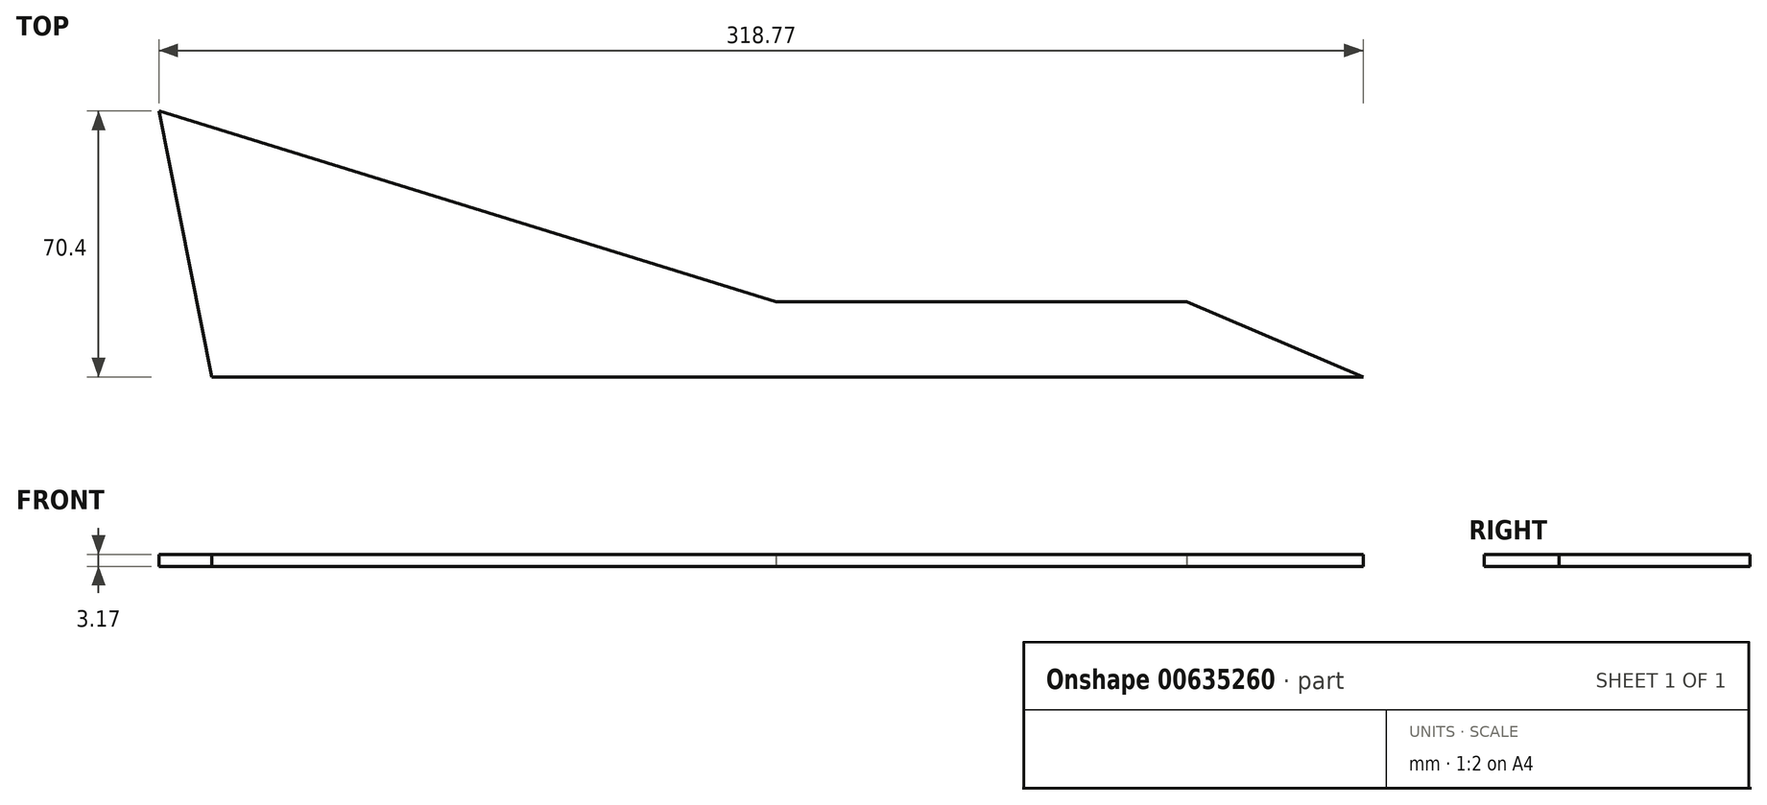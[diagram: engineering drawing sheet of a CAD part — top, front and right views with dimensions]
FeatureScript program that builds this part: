
annotation { "Feature Type Name" : "Feature", "Feature Type Description" : "" }
export const myFeature = defineFeature(function(context is Context, id is Id, definition is map)
    precondition{}
    {
        {
            var Q0;
            Q0=qCreatedBy(makeId("Top.planeOp"),FACE);
            var sketch = newSketch(context, id + "F0", { "sketchPlane" : qUnion([Q0])});
            skLineSegment(sketch, "E0", {"start": v(0, 0) * mm, "end": v(-304.8, 0) * mm});
            skLineSegment(sketch, "E1", {"start": v(-304.8, 0) * mm, "end": v(-318.77, 70.4) * mm});
            skLineSegment(sketch, "E2", {"start": v(-318.77, 70.4) * mm, "end": v(-155.47, 19.85) * mm});
            skLineSegment(sketch, "E3", {"start": v(-155.47, 19.85) * mm, "end": v(-46.76, 19.85) * mm});
            skLineSegment(sketch, "E4", {"start": v(-46.76, 19.85) * mm, "end": v(0, 0) * mm});
            skSolve(sketch);
        }
        {
            var Q0;
            Q0 = qSketchRegion(id + "F0", true);
            extrude(context, id + "F1", {"entities" : qUnion([Q0]), "depth" : 3.17 * mm, "offsetDistance" : 25.4 * mm});
        }
    });
